# Revit family: Door_BlastResistant_Ambico_MediumDuty-Double
name_source: partatom
category: Doors
units: mm (PartAtom-declared; Revit-internal decimal feet)

## family parameters
Always vertical = Yes
Classification Number = 23.30.10.21.37.14
Cut with Voids When Loaded = No
Host = Wall
Room Calculation Point = No
Shared = No

## types (1)
- as Specified
    ADA Compliant = Yes
    Backset = 0' - 3"
    Blast Resistance = as Specified
    Construction Details = http://www.arcat.com
    Description = Ambico Blast Resistant Medium Duty Steel Door - Pair as Specified
    Door Rabbet = 0' - 1 15/16"
    Expected Lifespan (Years) = 0
    Fire Rating = NFR
    Frame Finish = Metal - Steel - Ambico - Painted - Blue
    Frame Thickness = 0' - 5 3/4"
    Frame Width = 0' - 2"
    Function = Interior
    Green Building-LEED = http://www.arcat.com
    Handle Height = 3' - 4"
    Hardware Finish = Metal - Stainless Steel - Ambico - 4 Finish
    Heat Transfer Coefficient (U) = 0.1 BTU/(h·ft²·°F)
    Height = 7' - 0"
    Installation-Fabrication = http://www.ambico.com
    Keynote = 08300
    Maintenance Schedule (Months) = 0
    Manufacturer = Ambico Limited
    Manufacturer Fax = 800-465-8561
    Manufacturer Website = http://www.ambico.com
    Model = Blast Resistant Medium Duty Non Fire Rated
    Panel Height = 7' - 0"
    Panel Material = Metal - Steel - Ambico - Painted - Blue
    Panel Width = 3' - 0"
    Product Data = http://www.arcat.com
    R = 0.0000 (h·ft²·°F)/BTU
    RO Offset = 0' - 0"
    Rough Height = 7' - 0"
    Rough Width = 6' - 0"
    SHGC = 0
    Sales Information = http://www.ambico.com
    Send Message = http://www.arcat.com Limited&coid=40356&rep=119&fax=800-465-8561&mf=
    Solar Heat Gain Coefficient = 0
    Sound Transmission Class (STC) = 0
    Specification = http://www.arcat.com
    Stop Depth = 0' - 1 7/8"
    Thermal Resistance (R) = 0.0000 (h·ft²·°F)/BTU
    Thickness = 0' - 1 3/4"
    U = 0.1 BTU/(h·ft²·°F)
    URL = http://www.ambico.com
    VLT = 0
    Visual Light Transmittance = 0
    Wall Closure = By host
    Warranty Duration (Years) = 0
    Width = 6' - 0"

## geometry (parser evidence)
native form markers: Sweep x17
no freeform markers — native parametric forms only
